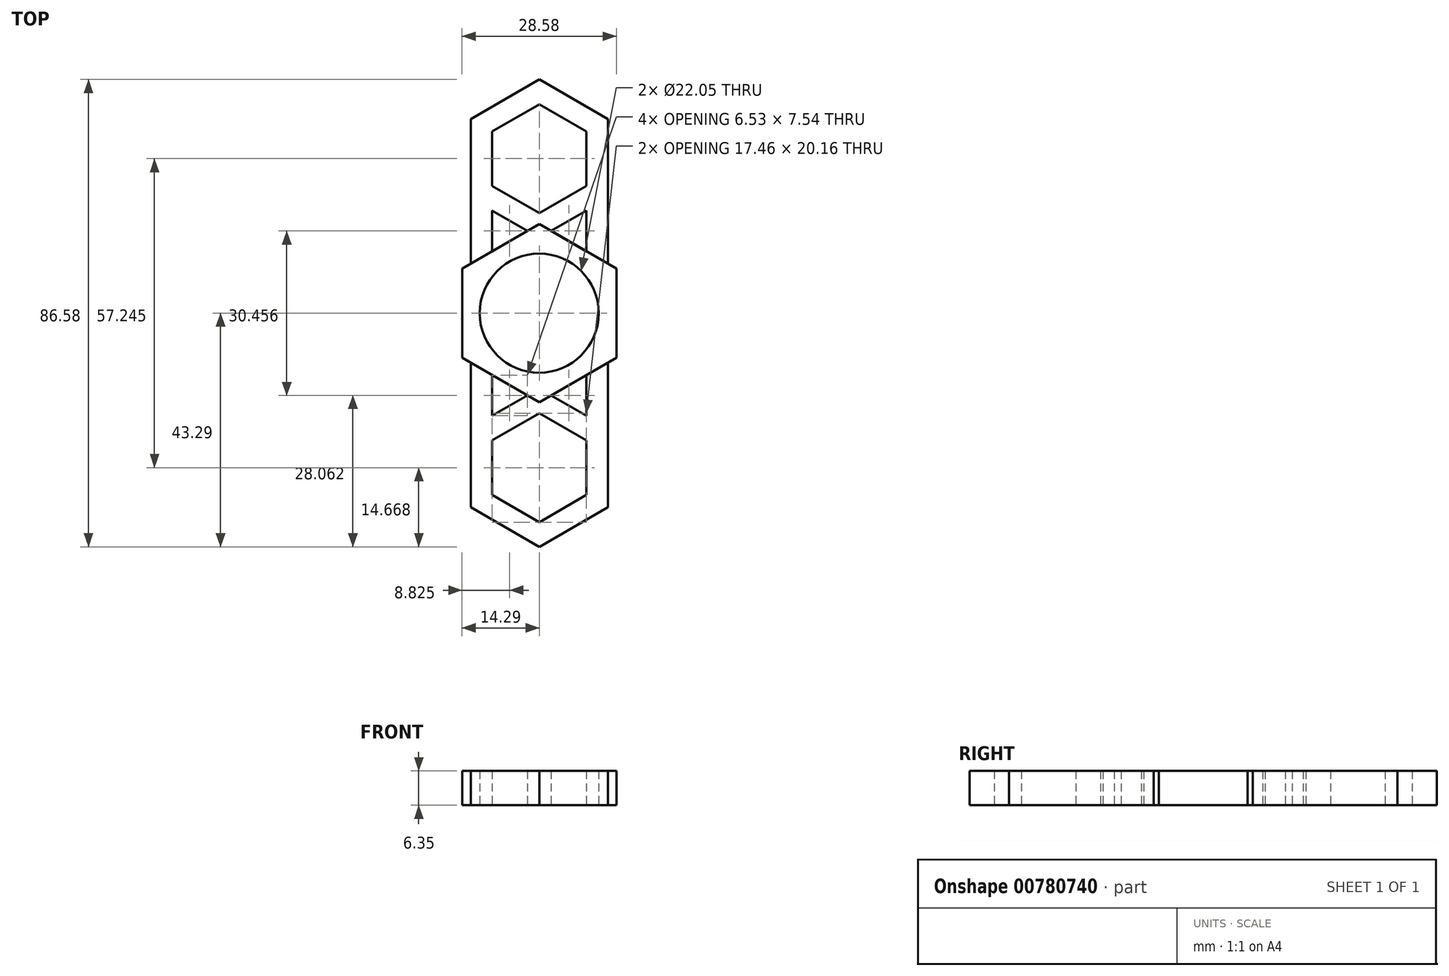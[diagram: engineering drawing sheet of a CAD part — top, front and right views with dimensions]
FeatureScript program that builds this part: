
annotation { "Feature Type Name" : "Feature", "Feature Type Description" : "" }
export const myFeature = defineFeature(function(context is Context, id is Id, definition is map)
    precondition{}
    {
        {
            var Q0;
            Q0=qCreatedBy(makeId("Top.planeOp"),FACE);
            var sketch = newSketch(context, id + "F0", { "sketchPlane" : qUnion([Q0])});
            skCircle(sketch, "E0", {"center": v(0, 0) * mm, "radius": 11.02 * mm});
            skCircle(sketch, "E1.cCircle", {"center": v(0, 28.62) * mm, "radius": 8.73 * mm, "construction": true});
            skLineSegment(sketch, "E1.0", {"start": v(8.73, 33.66) * mm, "end": v(8.73, 23.58) * mm});
            skLineSegment(sketch, "E1.1", {"start": v(8.73, 23.58) * mm, "end": v(0, 18.54) * mm});
            skLineSegment(sketch, "E1.2", {"start": v(0, 18.54) * mm, "end": v(-8.73, 23.58) * mm});
            skLineSegment(sketch, "E1.3", {"start": v(-8.73, 23.58) * mm, "end": v(-8.73, 33.66) * mm});
            skLineSegment(sketch, "E1.4", {"start": v(-8.73, 33.66) * mm, "end": v(0, 38.7) * mm});
            skLineSegment(sketch, "E1.5", {"start": v(0, 38.7) * mm, "end": v(8.73, 33.66) * mm});
            skPoint(sketch, "E1.0.midPoint", {"position": v(8.73, 28.62) * mm});
            skCircle(sketch, "E2.cCircle", {"center": v(0, 28.62) * mm, "radius": 12.7 * mm, "construction": true});
            skLineSegment(sketch, "E2.0", {"start": v(12.7, 35.95) * mm, "end": v(12.7, 21.3) * mm});
            skLineSegment(sketch, "E2.1", {"start": v(12.7, 21.3) * mm, "end": v(0, 13.96) * mm});
            skLineSegment(sketch, "E2.2", {"start": v(0, 13.96) * mm, "end": v(-12.7, 21.3) * mm});
            skLineSegment(sketch, "E2.3", {"start": v(-12.7, 21.3) * mm, "end": v(-12.7, 35.95) * mm});
            skLineSegment(sketch, "E2.4", {"start": v(-12.7, 35.95) * mm, "end": v(0, 43.29) * mm});
            skLineSegment(sketch, "E2.5", {"start": v(0, 43.29) * mm, "end": v(12.7, 35.95) * mm});
            skPoint(sketch, "E2.0.midPoint", {"position": v(12.7, 28.62) * mm});
            skCircle(sketch, "E3.cCircle", {"center": v(0, 0) * mm, "radius": 14.29 * mm, "construction": true});
            skLineSegment(sketch, "E3.0", {"start": v(14.29, 8.25) * mm, "end": v(14.29, -8.25) * mm});
            skLineSegment(sketch, "E3.1", {"start": v(14.29, -8.25) * mm, "end": v(0, -16.5) * mm});
            skLineSegment(sketch, "E3.2", {"start": v(0, -16.5) * mm, "end": v(-14.29, -8.25) * mm});
            skLineSegment(sketch, "E3.3", {"start": v(-14.29, -8.25) * mm, "end": v(-14.29, 8.25) * mm});
            skLineSegment(sketch, "E3.4", {"start": v(-14.29, 8.25) * mm, "end": v(0, 16.5) * mm});
            skLineSegment(sketch, "E3.5", {"start": v(0, 16.5) * mm, "end": v(14.29, 8.25) * mm});
            skPoint(sketch, "E3.0.midPoint", {"position": v(14.29, 0) * mm});
            skLineSegment(sketch, "E4", {"start": v(-12.7, 21.3) * mm, "end": v(-12.7, 9.17) * mm});
            skLineSegment(sketch, "E5", {"start": v(-8.73, 23.58) * mm, "end": v(-8.73, 11.46) * mm});
            skLineSegment(sketch, "E6", {"start": v(12.7, 21.3) * mm, "end": v(12.7, 9.17) * mm});
            skLineSegment(sketch, "E7", {"start": v(8.73, 23.58) * mm, "end": v(8.73, 11.46) * mm});
            skLineSegment(sketch, "E8", {"start": v(-12.7, 9.17) * mm, "end": v(-8.73, 11.46) * mm});
            skLineSegment(sketch, "E9", {"start": v(8.73, 11.46) * mm, "end": v(12.7, 9.17) * mm});
            skLineSegment(sketch, "E10", {"start": v(-12.7, 9.17) * mm, "end": v(-14.29, 8.25) * mm});
            skLineSegment(sketch, "E11", {"start": v(14.29, 8.25) * mm, "end": v(12.7, 9.17) * mm});
            skSolve(sketch);
        }
        {
            var Q0;
            {var subQ12=sQuery(id+"F0.wireOp",EDGE,"E1.1");Q0=makeQuery(id+"F0.imprint","IMPRINT",FACE,{"disambiguationData":[TD([[makeQuery(id+"F0.imprint","IMPRINT",EDGE,{"derivedFrom":subQ12}),1.0]])]});}
            var Q1;
            {var subQ0=sQuery(id+"F0.wireOp",EDGE,"E6");Q1=makeQuery(id+"F0.imprint","IMPRINT",FACE,{"disambiguationData":[TD([[makeQuery(id+"F0.imprint","IMPRINT",EDGE,{"derivedFrom":subQ0}),-1.0]])]});}
            var Q2;
            {var subQ0=sQuery(id+"F0.wireOp",EDGE,"E2.2");var subQ1=sQuery(id+"F0.wireOp",EDGE,"E2.1");var subQ2=makeQuery(id+"F0.imprint","INTERSECT",VERTEX,{"derivedFrom":[subQ1,subQ0]});Q2=makeQuery(id+"F0.imprint","IMPRINT",FACE,{"disambiguationData":[TD([[makeQuery(id+"F0.imprint","IMPRINT",EDGE,{"disambiguationData":[TD([[subQ2,1.0]])],"derivedFrom":subQ1}),-1.0]])]});}
            var Q3;
            {var subQ0=sQuery(id+"F0.wireOp",EDGE,"E4");Q3=makeQuery(id+"F0.imprint","IMPRINT",FACE,{"disambiguationData":[TD([[makeQuery(id+"F0.imprint","IMPRINT",EDGE,{"derivedFrom":subQ0}),1.0]])]});}
            var Q4;
            Q4=makeQuery(id+"F0.imprint","IMPRINT",FACE,{"disambiguationData":[TD([[makeQuery(id+"F0.imprint","IMPRINT",EDGE,{"derivedFrom":sQuery(id+"F0.wireOp",EDGE,"E0")}),-1.0]])]});
            var Q5;
            {var subQ9=sQuery(id+"F0.wireOp",EDGE,"E1.0");Q5=makeQuery(id+"F0.imprint","IMPRINT",FACE,{"disambiguationData":[TD([[makeQuery(id+"F0.imprint","IMPRINT",EDGE,{"derivedFrom":subQ9}),1.0]])]});}
            extrude(context, id + "F1", {"entities" : qUnion([Q0, Q1, Q2, Q3, Q4, Q5]), "depth" : 6.35 * mm, "offsetDistance" : 25.4 * mm});
        }
        {
            var Q0;
            Q0=makeQuery(id+"F1.opExtrude","SWEPT_BODY",BODY,{"disambiguationData":[OSD([sQuery(id+"F0.wireOp",EDGE,"E0"),sQuery(id+"F0.wireOp",EDGE,"E1.0"),sQuery(id+"F0.wireOp",EDGE,"E1.1"),sQuery(id+"F0.wireOp",EDGE,"E1.2"),sQuery(id+"F0.wireOp",EDGE,"E1.3"),sQuery(id+"F0.wireOp",EDGE,"E1.4"),sQuery(id+"F0.wireOp",EDGE,"E1.5"),sQuery(id+"F0.wireOp",EDGE,"E2.0"),sQuery(id+"F0.wireOp",EDGE,"E2.1"),sQuery(id+"F0.wireOp",EDGE,"E2.2"),sQuery(id+"F0.wireOp",EDGE,"E2.3"),sQuery(id+"F0.wireOp",EDGE,"E2.4"),sQuery(id+"F0.wireOp",EDGE,"E2.5"),sQuery(id+"F0.wireOp",EDGE,"E3.0"),sQuery(id+"F0.wireOp",EDGE,"E3.1"),sQuery(id+"F0.wireOp",EDGE,"E3.2"),sQuery(id+"F0.wireOp",EDGE,"E3.3"),sQuery(id+"F0.wireOp",EDGE,"E3.4"),sQuery(id+"F0.wireOp",EDGE,"E3.5"),sQuery(id+"F0.wireOp",EDGE,"E4"),sQuery(id+"F0.wireOp",EDGE,"E5"),sQuery(id+"F0.wireOp",EDGE,"E6"),sQuery(id+"F0.wireOp",EDGE,"E7")])]});
            var Q1;
            Q1=makeQuery(id+"F1.opExtrude","CAP_EDGE",EDGE,{"disambiguationData":[OSD([sQuery(id+"F0.wireOp",EDGE,"E0")])],"isStart":false});
            circularPattern(context, id + "F2", {"entities" : qUnion([Q0]), "axis" : qUnion([Q1]), "angle" : 360 * degree, "instanceCount" : 2, "equalSpace" : true});
        }
    });
